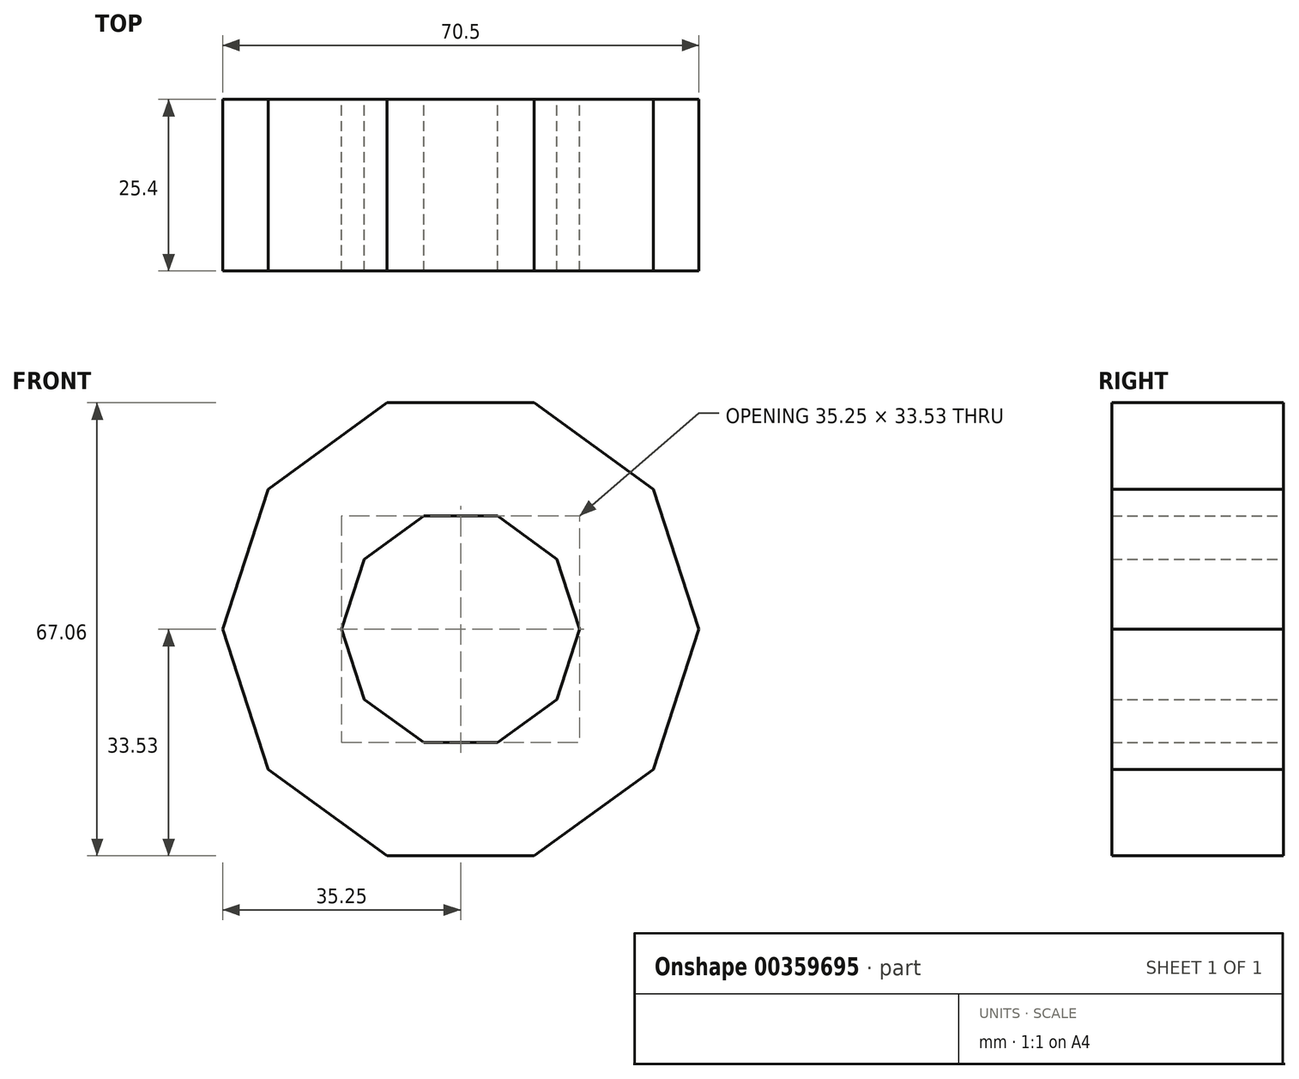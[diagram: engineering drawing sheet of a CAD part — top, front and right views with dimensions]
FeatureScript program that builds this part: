
annotation { "Feature Type Name" : "Feature", "Feature Type Description" : "" }
export const myFeature = defineFeature(function(context is Context, id is Id, definition is map)
    precondition{}
    {
        {
            var Q0;
            Q0=qCreatedBy(makeId("Front.planeOp"),FACE);
            var sketch = newSketch(context, id + "F0", { "sketchPlane" : qUnion([Q0])});
            skLineSegment(sketch, "E0", {"start": v(0, 0) * mm, "end": v(0, 33.53) * mm});
            skLineSegment(sketch, "E1", {"start": v(0, 0) * mm, "end": v(0, 16.76) * mm});
            skCircle(sketch, "E2.cCircle", {"center": v(0, 0) * mm, "radius": 33.53 * mm, "construction": true});
            skLineSegment(sketch, "E2.0", {"start": v(-10.9, 33.53) * mm, "end": v(10.9, 33.53) * mm});
            skLineSegment(sketch, "E2.1", {"start": v(10.9, 33.53) * mm, "end": v(28.52, 20.72) * mm});
            skLineSegment(sketch, "E2.2", {"start": v(28.52, 20.72) * mm, "end": v(35.25, 0) * mm});
            skLineSegment(sketch, "E2.3", {"start": v(35.25, 0) * mm, "end": v(28.52, -20.72) * mm});
            skLineSegment(sketch, "E2.4", {"start": v(28.52, -20.72) * mm, "end": v(10.9, -33.53) * mm});
            skLineSegment(sketch, "E2.5", {"start": v(10.9, -33.53) * mm, "end": v(-10.9, -33.53) * mm});
            skLineSegment(sketch, "E2.6", {"start": v(-10.9, -33.53) * mm, "end": v(-28.52, -20.72) * mm});
            skLineSegment(sketch, "E2.7", {"start": v(-28.52, -20.72) * mm, "end": v(-35.25, 0) * mm});
            skLineSegment(sketch, "E2.8", {"start": v(-35.25, 0) * mm, "end": v(-28.52, 20.72) * mm});
            skLineSegment(sketch, "E2.9", {"start": v(-28.52, 20.72) * mm, "end": v(-10.9, 33.53) * mm});
            skPoint(sketch, "E2.0.midPoint", {"position": v(0, 33.53) * mm});
            skCircle(sketch, "E3.cCircle", {"center": v(0, 0) * mm, "radius": 16.76 * mm, "construction": true});
            skLineSegment(sketch, "E3.0", {"start": v(-5.45, 16.76) * mm, "end": v(5.45, 16.76) * mm});
            skLineSegment(sketch, "E3.1", {"start": v(5.45, 16.76) * mm, "end": v(14.26, 10.36) * mm});
            skLineSegment(sketch, "E3.2", {"start": v(14.26, 10.36) * mm, "end": v(17.63, 0) * mm});
            skLineSegment(sketch, "E3.3", {"start": v(17.63, 0) * mm, "end": v(14.26, -10.36) * mm});
            skLineSegment(sketch, "E3.4", {"start": v(14.26, -10.36) * mm, "end": v(5.45, -16.76) * mm});
            skLineSegment(sketch, "E3.5", {"start": v(5.45, -16.76) * mm, "end": v(-5.45, -16.76) * mm});
            skLineSegment(sketch, "E3.6", {"start": v(-5.45, -16.76) * mm, "end": v(-14.26, -10.36) * mm});
            skLineSegment(sketch, "E3.7", {"start": v(-14.26, -10.36) * mm, "end": v(-17.63, 0) * mm});
            skLineSegment(sketch, "E3.8", {"start": v(-17.63, 0) * mm, "end": v(-14.26, 10.36) * mm});
            skLineSegment(sketch, "E3.9", {"start": v(-14.26, 10.36) * mm, "end": v(-5.45, 16.76) * mm});
            skPoint(sketch, "E3.0.midPoint", {"position": v(0, 16.76) * mm});
            skSolve(sketch);
        }
        {
            var Q0;
            {var subQ3=sQuery(id+"F0.wireOp",EDGE,"E2.1");Q0=makeQuery(id+"F0.imprint","IMPRINT",FACE,{"disambiguationData":[TD([[makeQuery(id+"F0.imprint","IMPRINT",EDGE,{"derivedFrom":subQ3}),-1.0]])]});}
            extrude(context, id + "F1", {"entities" : qUnion([Q0]), "depth" : 25.4 * mm});
        }
    });
